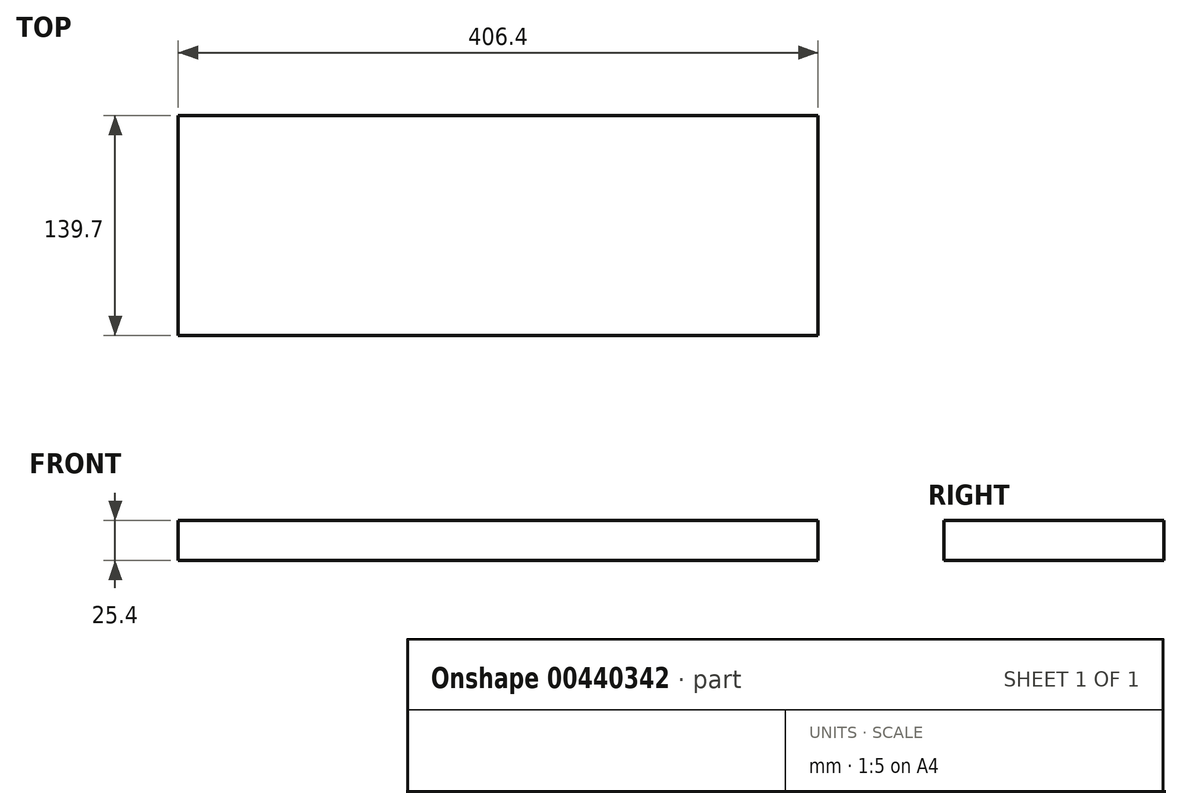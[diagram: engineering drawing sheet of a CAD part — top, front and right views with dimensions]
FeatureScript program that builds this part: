
annotation { "Feature Type Name" : "Feature", "Feature Type Description" : "" }
export const myFeature = defineFeature(function(context is Context, id is Id, definition is map)
    precondition{}
    {
        {
            var Q0;
            Q0=qCreatedBy(makeId("Top.planeOp"),FACE);
            var sketch = newSketch(context, id + "F0", { "sketchPlane" : qUnion([Q0])});
            skLineSegment(sketch, "E0.bottom", {"start": v(-203.2, 69.85) * mm, "end": v(203.2, 69.85) * mm});
            skLineSegment(sketch, "E0.top", {"start": v(-203.2, -69.85) * mm, "end": v(203.2, -69.85) * mm});
            skLineSegment(sketch, "E0.left", {"start": v(-203.2, 69.85) * mm, "end": v(-203.2, -69.85) * mm});
            skLineSegment(sketch, "E0.right", {"start": v(203.2, 69.85) * mm, "end": v(203.2, -69.85) * mm});
            skPoint(sketch, "E0.middle", {"position": v(0, 0) * mm});
            skSolve(sketch);
        }
        {
            var Q0;
            Q0=makeQuery(id+"F0.imprint","IMPRINT",FACE,{"disambiguationData":[TD([[makeQuery(id+"F0.imprint","IMPRINT",EDGE,{"derivedFrom":sQuery(id+"F0.wireOp",EDGE,"E0.bottom")}),-1.0]])]});
            extrude(context, id + "F1", {"entities" : qUnion([Q0]), "depth" : 25.4 * mm});
        }
    });
